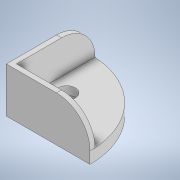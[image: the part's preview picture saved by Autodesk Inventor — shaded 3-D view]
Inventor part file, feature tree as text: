
AUTODESK INVENTOR PART (.ipt)
format: ipt  version: 2020 (Build 240168000, 168)  size: 143,360 bytes
history: native  units: mm
features: sketch x5, extrude x4, fillet x2, hole x1
ambient origin geometry x8: Origin, YZ Plane, XZ Plane, XY Plane, X Axis, Y Axis, Z Axis, Center Point
bodies: Solid1 (feature_tree)
feature tree (12):
  extrude  "Extrusion1"  Depth=7.0mm TaperAngle=0.0deg
  extrude  "Extrusion2"  Depth=3.0mm
  extrude  "Extrusion3"  Depth=3.0mm
  extrude  "Extrusion4"  Depth=20.0mm TaperAngle=0.0deg
  hole  "Hole1"  [1 undecoded]
  fillet  "Fillet1"  Radius=50.0mm
  fillet  "Fillet2"  Radius=50.0mm
  sketch  "Sketch1"  dims[d0=100.0mm d1=7.0mm d2=0.0mm]
  sketch  "Sketch2"  dims[d3=50.0mm d4=3.0mm]
  sketch  "Sketch3"  dims[d5=20.0mm d6=0.0mm d7=3.0mm]
  sketch  "Sketch4"  dims[d8=50.0mm d9=20.0mm d10=0.0mm]
  sketch  "Sketch5"  dims[d11=50.0mm d12=100.0mm d13=50.0mm d14=50.0mm d15=7.0mm d16=0.0mm d17=6.5mm d18=6.0mm d19=10.5mm d20=5.0mm d21=90.0deg d22=8.0mm d23=20.594885mm d24=10.0mm d25=20.0mm d26=20.0mm d27=20.0mm]
note: 1 required parameter value undecoded (feature->parameter linkage not recoverable at this tier; creation-order binding heuristic only, values carry confidence <= 0.55)
